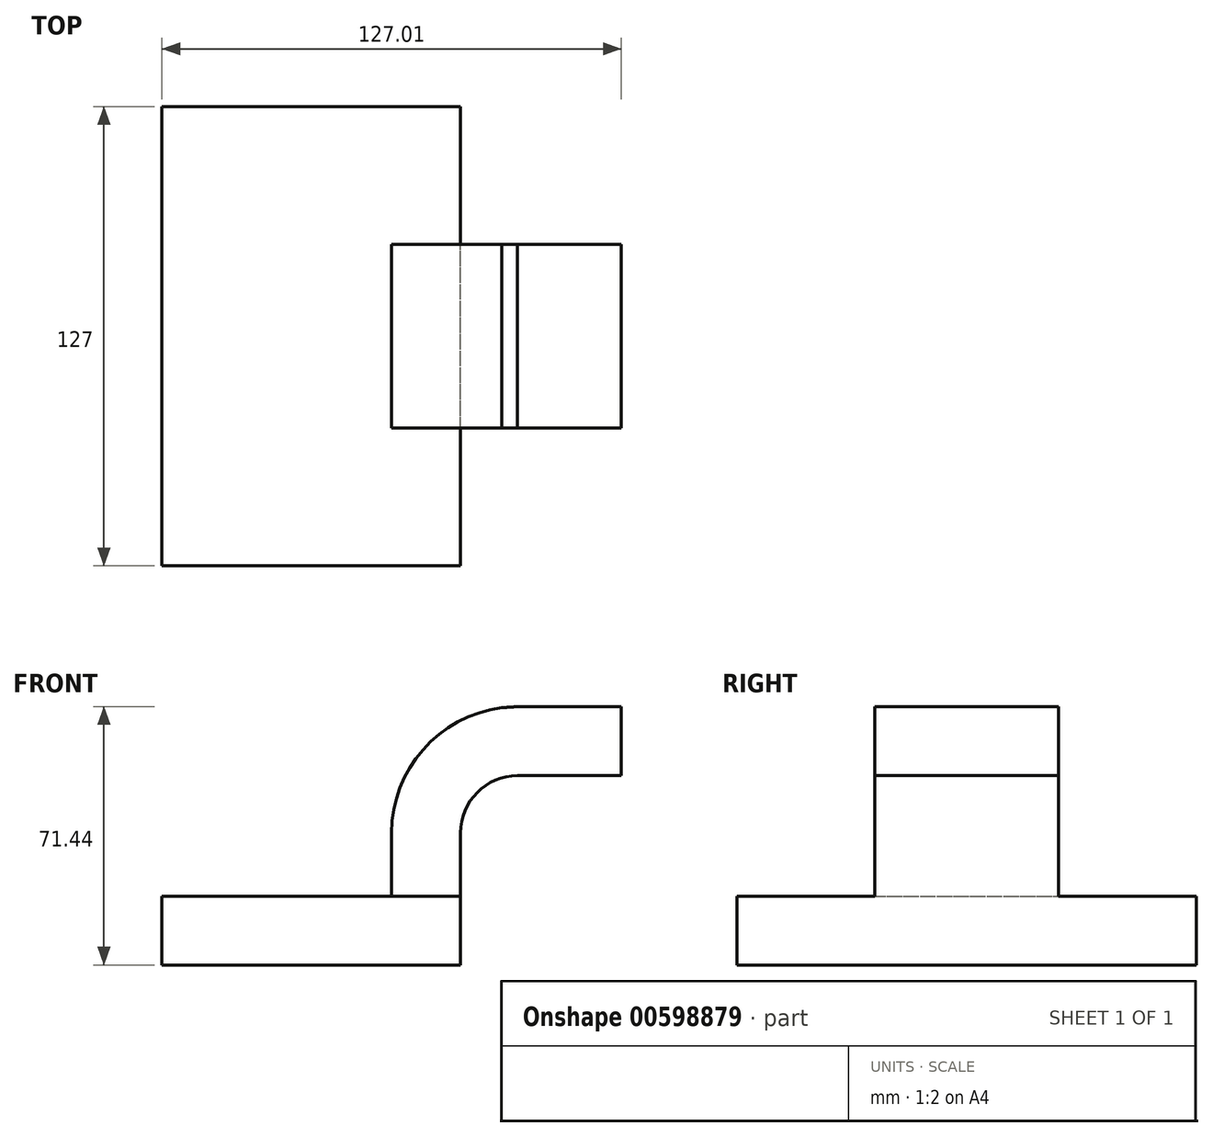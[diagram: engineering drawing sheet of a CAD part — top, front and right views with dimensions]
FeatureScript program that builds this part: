
annotation { "Feature Type Name" : "Feature", "Feature Type Description" : "" }
export const myFeature = defineFeature(function(context is Context, id is Id, definition is map)
    precondition{}
    {
        {
            var Q0;
            Q0=qCreatedBy(makeId("Front.planeOp"),FACE);
            var sketch = newSketch(context, id + "F0", { "sketchPlane" : qUnion([Q0])});
            skLineSegment(sketch, "E0.bottom", {"start": v(41.28, -9.52) * mm, "end": v(-41.28, -9.53) * mm});
            skLineSegment(sketch, "E0.top", {"start": v(41.28, 9.53) * mm, "end": v(-41.28, 9.53) * mm});
            skLineSegment(sketch, "E0.left", {"start": v(41.28, -9.52) * mm, "end": v(41.28, 9.53) * mm});
            skLineSegment(sketch, "E0.right", {"start": v(-41.28, -9.53) * mm, "end": v(-41.28, 9.53) * mm});
            skPoint(sketch, "E0.middle", {"position": v(0, 0) * mm});
            skLineSegment(sketch, "E1.bottom", {"start": v(111.12, 66.68) * mm, "end": v(60.32, 66.68) * mm});
            skLineSegment(sketch, "E1.top", {"start": v(111.12, 38.1) * mm, "end": v(60.33, 38.1) * mm});
            skLineSegment(sketch, "E1.left", {"start": v(111.12, 66.67) * mm, "end": v(111.12, 38.1) * mm});
            skLineSegment(sketch, "E1.right", {"start": v(60.32, 66.67) * mm, "end": v(60.33, 38.1) * mm});
            skPoint(sketch, "E1.middle", {"position": v(85.72, 52.39) * mm});
            skLineSegment(sketch, "E2", {"start": v(41.28, 9.53) * mm, "end": v(41.28, 26.99) * mm});
            skArc(sketch, "E3", {"start": v(41.28, 26.99) * mm, "mid": v(45.88, 38.17) * mm, "end": v(57.03, 42.86) * mm});
            skLineSegment(sketch, "E4", {"start": v(57.03, 42.86) * mm, "end": v(85.72, 42.86) * mm});
            skLineSegment(sketch, "E5.0", {"start": v(56.98, 61.91) * mm, "end": v(85.72, 61.91) * mm});
            skArc(sketch, "E5.1", {"start": v(22.23, 26.99) * mm, "mid": v(32.4, 51.62) * mm, "end": v(56.98, 61.91) * mm});
            skLineSegment(sketch, "E5.2", {"start": v(22.22, 9.53) * mm, "end": v(22.22, 26.99) * mm});
            skLineSegment(sketch, "E6", {"start": v(85.72, 38.1) * mm, "end": v(85.72, 66.68) * mm});
            skFitSpline(sketch, "E7", {"points": [v(-41.28, 9.52) * mm, v(56.98, 61.91) * mm], "startDerivative": vector(0.13, 92.75) * mm, "endDerivative": vector(111.54, 5.71) * mm});
            skSolve(sketch);
        }
        {
            var Q0;
            Q0=makeQuery(id+"F0.imprint","IMPRINT",FACE,{"disambiguationData":[TD([[makeQuery(id+"F0.imprint","IMPRINT",EDGE,{"derivedFrom":sQuery(id+"F0.wireOp",EDGE,"E0.bottom")}),-1.0]])]});
            extrude(context, id + "F1", {"entities" : qUnion([Q0]), "endBound" : BoundingType.SYMMETRIC, "depth" : 127 * mm, "offsetDistance" : 25.4 * mm});
        }
        {
            var Q0;
            {var subQ1=sQuery(id+"F0.wireOp",EDGE,"E2");Q0=makeQuery(id+"F0.imprint","IMPRINT",FACE,{"disambiguationData":[TD([[makeQuery(id+"F0.imprint","IMPRINT",EDGE,{"derivedFrom":subQ1}),1.0]])]});}
            var Q1;
            {var subQ0=sQuery(id+"F0.wireOp",EDGE,"E5.0");var subQ1=sQuery(id+"F0.wireOp",EDGE,"E1.right");var subQ2=makeQuery(id+"F0.imprint","INTERSECT",VERTEX,{"derivedFrom":[subQ1,subQ0]});Q1=makeQuery(id+"F0.imprint","IMPRINT",FACE,{"disambiguationData":[TD([[makeQuery(id+"F0.imprint","IMPRINT",EDGE,{"disambiguationData":[TD([[subQ2,-1.0]])],"derivedFrom":subQ1}),1.0]])]});}
            extrude(context, id + "F2", {"entities" : qUnion([Q0, Q1]), "operationType" : NewBodyOperationType.ADD, "endBound" : BoundingType.SYMMETRIC, "depth" : 50.8 * mm, "offsetDistance" : 25.4 * mm});
        }
    });
